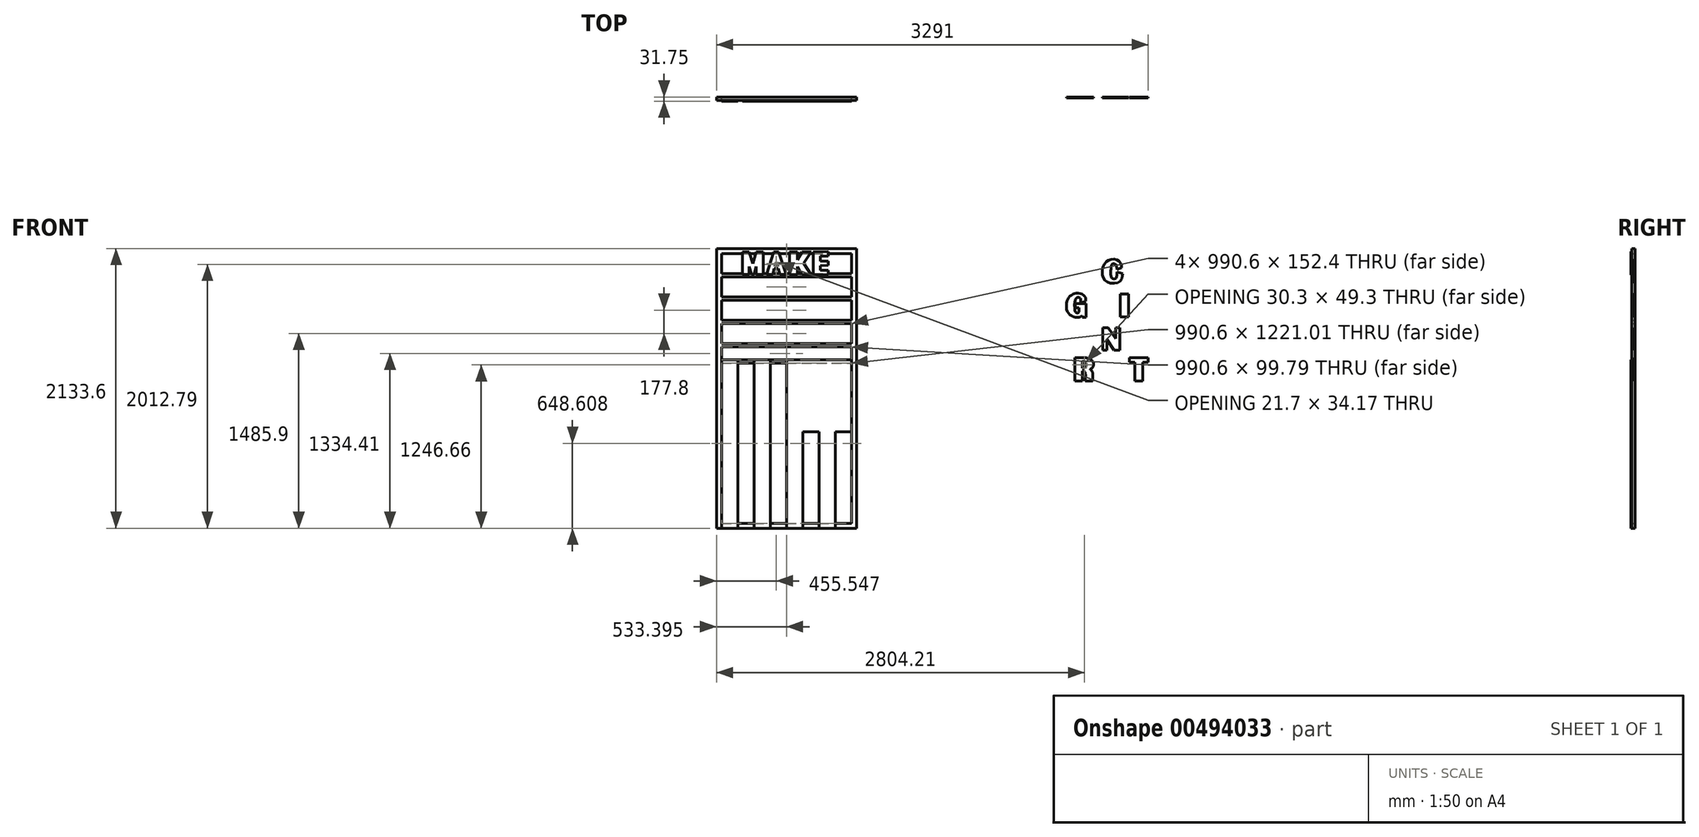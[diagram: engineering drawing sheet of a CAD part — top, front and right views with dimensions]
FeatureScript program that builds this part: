
annotation { "Feature Type Name" : "Feature", "Feature Type Description" : "" }
export const myFeature = defineFeature(function(context is Context, id is Id, definition is map)
    precondition{}
    {
        {
            var Q0;
            Q0=qCreatedBy(makeId("Front.planeOp"),FACE);
            var sketch = newSketch(context, id + "F0", { "sketchPlane" : qUnion([Q0])});
            skLineSegment(sketch, "E0.bottom", {"start": v(-657.23, 1067.61) * mm, "end": v(409.57, 1067.61) * mm});
            skLineSegment(sketch, "E0.top", {"start": v(-657.23, -1065.99) * mm, "end": v(409.58, -1065.99) * mm});
            skLineSegment(sketch, "E0.left", {"start": v(-657.23, 1067.61) * mm, "end": v(-657.23, -1065.99) * mm});
            skLineSegment(sketch, "E0.right", {"start": v(409.57, 1067.61) * mm, "end": v(409.57, -1065.99) * mm});
            skLineSegment(sketch, "E1.0", {"start": v(-619.13, 1029.51) * mm, "end": v(371.47, 1029.51) * mm});
            skLineSegment(sketch, "E1.1", {"start": v(-619.13, 1029.51) * mm, "end": v(-619.12, -1027.89) * mm});
            skLineSegment(sketch, "E1.2", {"start": v(-619.13, -1027.89) * mm, "end": v(371.48, -1027.89) * mm});
            skLineSegment(sketch, "E1.3", {"start": v(371.47, 1029.51) * mm, "end": v(371.47, -1027.89) * mm});
            skPoint(sketch, "E2.endSnap0", {"position": v(409.57, 0.81) * mm});
            skLineSegment(sketch, "E3", {"start": v(-619.13, 877.11) * mm, "end": v(371.47, 877.11) * mm});
            skLineSegment(sketch, "E4", {"start": v(371.47, 851.71) * mm, "end": v(-619.13, 851.71) * mm});
            skLineSegment(sketch, "E5", {"start": v(-619.13, 699.31) * mm, "end": v(371.47, 699.31) * mm});
            skLineSegment(sketch, "E6", {"start": v(-619.13, 673.91) * mm, "end": v(371.47, 673.91) * mm});
            skLineSegment(sketch, "E7", {"start": v(-619.13, 521.51) * mm, "end": v(371.47, 521.51) * mm});
            skLineSegment(sketch, "E8", {"start": v(-619.13, 496.11) * mm, "end": v(371.47, 496.11) * mm});
            skLineSegment(sketch, "E9", {"start": v(-619.13, 343.71) * mm, "end": v(371.47, 343.71) * mm});
            skLineSegment(sketch, "E10", {"start": v(-619.13, 318.31) * mm, "end": v(371.47, 318.31) * mm});
            skLineSegment(sketch, "E11", {"start": v(-619.13, 218.53) * mm, "end": v(371.47, 218.53) * mm});
            skPoint(sketch, "E12.startSnap0", {"position": v(-123.83, 1067.61) * mm});
            skLineSegment(sketch, "E13", {"start": v(-123.83, 218.53) * mm, "end": v(-123.83, -330.69) * mm});
            skLineSegment(sketch, "E14", {"start": v(-123.83, -330.69) * mm, "end": v(371.47, -330.69) * mm});
            skLineSegment(sketch, "E15", {"start": v(-619.12, 193.13) * mm, "end": v(-495.3, 193.13) * mm});
            skLineSegment(sketch, "E16", {"start": v(247.65, -330.69) * mm, "end": v(247.65, -1027.89) * mm});
            skLineSegment(sketch, "E17", {"start": v(-123.83, -330.69) * mm, "end": v(-123.82, -1027.89) * mm});
            skLineSegment(sketch, "E18", {"start": v(0, -330.69) * mm, "end": v(0, -1027.89) * mm});
            skLineSegment(sketch, "E19", {"start": v(123.82, -330.69) * mm, "end": v(123.83, -1027.89) * mm});
            skLineSegment(sketch, "E20", {"start": v(-247.65, 193.13) * mm, "end": v(-247.65, -1027.89) * mm});
            skLineSegment(sketch, "E21", {"start": v(-371.48, 193.13) * mm, "end": v(-371.47, -1027.89) * mm});
            skLineSegment(sketch, "E22", {"start": v(-495.3, 193.13) * mm, "end": v(-495.3, -1027.89) * mm});
            skLineSegment(sketch, "E23", {"start": v(-495.3, 193.13) * mm, "end": v(-495.3, 218.53) * mm});
            skLineSegment(sketch, "E24", {"start": v(-371.48, 193.13) * mm, "end": v(-371.48, 218.53) * mm});
            skLineSegment(sketch, "E25", {"start": v(-247.65, 193.13) * mm, "end": v(-247.65, 218.53) * mm});
            skPoint(sketch, "E26.orphan", {"position": v(-123.83, 193.13) * mm});
            skLineSegment(sketch, "E27.trimOffspring", {"start": v(-371.48, 193.13) * mm, "end": v(-247.65, 193.13) * mm});
            skLineSegment(sketch, "E28", {"start": v(-495.3, 193.13) * mm, "end": v(-371.48, 193.13) * mm});
            skLineSegment(sketch, "E29", {"start": v(-247.65, 193.13) * mm, "end": v(-123.83, 193.13) * mm});
            skLineSegment(sketch, "E30", {"start": v(-123.83, 193.13) * mm, "end": v(371.47, 193.13) * mm});
            skLineSegment(sketch, "E31", {"start": v(-619.12, -1027.89) * mm, "end": v(-619.12, -1065.99) * mm});
            skLineSegment(sketch, "E32", {"start": v(-495.3, -1027.89) * mm, "end": v(-495.3, -1065.99) * mm});
            skLineSegment(sketch, "E33", {"start": v(-371.47, -1027.89) * mm, "end": v(-371.47, -1065.99) * mm});
            skLineSegment(sketch, "E34", {"start": v(-247.65, -1027.89) * mm, "end": v(-247.65, -1065.99) * mm});
            skLineSegment(sketch, "E35", {"start": v(-123.83, -1027.89) * mm, "end": v(-123.83, -1065.99) * mm});
            skLineSegment(sketch, "E36", {"start": v(0, -1027.89) * mm, "end": v(0, -1065.99) * mm});
            skLineSegment(sketch, "E37", {"start": v(123.83, -1027.89) * mm, "end": v(123.83, -1065.99) * mm});
            skLineSegment(sketch, "E38", {"start": v(247.65, -1027.89) * mm, "end": v(247.65, -1065.99) * mm});
            skLineSegment(sketch, "E39", {"start": v(371.48, -1027.89) * mm, "end": v(371.48, -1065.99) * mm});
            skSolve(sketch);
        }
        {
            var Q0;
            Q0=makeQuery(id+"F0.imprint","IMPRINT",FACE,{"disambiguationData":[TD([[makeQuery(id+"F0.imprint","IMPRINT",EDGE,{"derivedFrom":sQuery(id+"F0.wireOp",EDGE,"E0.bottom")}),-1.0]])]});
            var Q1;
            {var subQ0=sQuery(id+"F0.wireOp",EDGE,"E3");Q1=makeQuery(id+"F0.imprint","IMPRINT",FACE,{"disambiguationData":[TD([[makeQuery(id+"F0.imprint","IMPRINT",EDGE,{"derivedFrom":subQ0}),-1.0]])]});}
            var Q2;
            {var subQ0=sQuery(id+"F0.wireOp",EDGE,"E5");Q2=makeQuery(id+"F0.imprint","IMPRINT",FACE,{"disambiguationData":[TD([[makeQuery(id+"F0.imprint","IMPRINT",EDGE,{"derivedFrom":subQ0}),-1.0]])]});}
            var Q3;
            {var subQ0=sQuery(id+"F0.wireOp",EDGE,"E7");Q3=makeQuery(id+"F0.imprint","IMPRINT",FACE,{"disambiguationData":[TD([[makeQuery(id+"F0.imprint","IMPRINT",EDGE,{"derivedFrom":subQ0}),-1.0]])]});}
            var Q4;
            {var subQ0=sQuery(id+"F0.wireOp",EDGE,"E9");Q4=makeQuery(id+"F0.imprint","IMPRINT",FACE,{"disambiguationData":[TD([[makeQuery(id+"F0.imprint","IMPRINT",EDGE,{"derivedFrom":subQ0}),-1.0]])]});}
            var Q5;
            {var subQ3=sQuery(id+"F0.wireOp",EDGE,"E15");Q5=makeQuery(id+"F0.imprint","IMPRINT",FACE,{"disambiguationData":[TD([[makeQuery(id+"F0.imprint","IMPRINT",EDGE,{"derivedFrom":subQ3}),1.0]])]});}
            var Q6;
            {var subQ0=sQuery(id+"F0.wireOp",EDGE,"E23");Q6=makeQuery(id+"F0.imprint","IMPRINT",FACE,{"disambiguationData":[TD([[makeQuery(id+"F0.imprint","IMPRINT",EDGE,{"derivedFrom":subQ0}),-1.0]])]});}
            var Q7;
            {var subQ0=sQuery(id+"F0.wireOp",EDGE,"E24");Q7=makeQuery(id+"F0.imprint","IMPRINT",FACE,{"disambiguationData":[TD([[makeQuery(id+"F0.imprint","IMPRINT",EDGE,{"derivedFrom":subQ0}),-1.0]])]});}
            var Q8;
            {var subQ3=sQuery(id+"F0.wireOp",EDGE,"E25");Q8=makeQuery(id+"F0.imprint","IMPRINT",FACE,{"disambiguationData":[TD([[makeQuery(id+"F0.imprint","IMPRINT",EDGE,{"derivedFrom":subQ3}),-1.0]])]});}
            var Q9;
            {var subQ3=sQuery(id+"F0.wireOp",EDGE,"E30");Q9=makeQuery(id+"F0.imprint","IMPRINT",FACE,{"disambiguationData":[TD([[makeQuery(id+"F0.imprint","IMPRINT",EDGE,{"derivedFrom":subQ3}),1.0]])]});}
            var Q10;
            {var subQ0=sQuery(id+"F0.wireOp",EDGE,"E38");Q10=makeQuery(id+"F0.imprint","IMPRINT",FACE,{"disambiguationData":[TD([[makeQuery(id+"F0.imprint","IMPRINT",EDGE,{"derivedFrom":subQ0}),1.0]])]});}
            var Q11;
            {var subQ0=sQuery(id+"F0.wireOp",EDGE,"E37");Q11=makeQuery(id+"F0.imprint","IMPRINT",FACE,{"disambiguationData":[TD([[makeQuery(id+"F0.imprint","IMPRINT",EDGE,{"derivedFrom":subQ0}),1.0]])]});}
            var Q12;
            {var subQ0=sQuery(id+"F0.wireOp",EDGE,"E36");Q12=makeQuery(id+"F0.imprint","IMPRINT",FACE,{"disambiguationData":[TD([[makeQuery(id+"F0.imprint","IMPRINT",EDGE,{"derivedFrom":subQ0}),1.0]])]});}
            var Q13;
            {var subQ0=sQuery(id+"F0.wireOp",EDGE,"E35");Q13=makeQuery(id+"F0.imprint","IMPRINT",FACE,{"disambiguationData":[TD([[makeQuery(id+"F0.imprint","IMPRINT",EDGE,{"derivedFrom":subQ0}),1.0]])]});}
            var Q14;
            {var subQ0=sQuery(id+"F0.wireOp",EDGE,"E34");Q14=makeQuery(id+"F0.imprint","IMPRINT",FACE,{"disambiguationData":[TD([[makeQuery(id+"F0.imprint","IMPRINT",EDGE,{"derivedFrom":subQ0}),1.0]])]});}
            var Q15;
            {var subQ0=sQuery(id+"F0.wireOp",EDGE,"E33");Q15=makeQuery(id+"F0.imprint","IMPRINT",FACE,{"disambiguationData":[TD([[makeQuery(id+"F0.imprint","IMPRINT",EDGE,{"derivedFrom":subQ0}),1.0]])]});}
            var Q16;
            {var subQ0=sQuery(id+"F0.wireOp",EDGE,"E32");Q16=makeQuery(id+"F0.imprint","IMPRINT",FACE,{"disambiguationData":[TD([[makeQuery(id+"F0.imprint","IMPRINT",EDGE,{"derivedFrom":subQ0}),1.0]])]});}
            var Q17;
            {var subQ0=sQuery(id+"F0.wireOp",EDGE,"E31");Q17=makeQuery(id+"F0.imprint","IMPRINT",FACE,{"disambiguationData":[TD([[makeQuery(id+"F0.imprint","IMPRINT",EDGE,{"derivedFrom":subQ0}),1.0]])]});}
            extrude(context, id + "F1", {"entities" : qUnion([Q0, Q1, Q2, Q3, Q4, Q5, Q6, Q7, Q8, Q9, Q10, Q11, Q12, Q13, Q14, Q15, Q16, Q17]), "depth" : 25.4 * mm});
        }
        {
            var Q0;
            Q0=makeQuery(id+"F1.opExtrude","CAP_FACE",FACE,{"disambiguationData":[OSD([sQuery(id+"F0.wireOp",EDGE,"E0.bottom"),sQuery(id+"F0.wireOp",EDGE,"E0.top"),sQuery(id+"F0.wireOp",EDGE,"E0.left"),sQuery(id+"F0.wireOp",EDGE,"E0.right"),sQuery(id+"F0.wireOp",EDGE,"E1.0"),sQuery(id+"F0.wireOp",EDGE,"E1.1"),sQuery(id+"F0.wireOp",EDGE,"E1.2"),sQuery(id+"F0.wireOp",EDGE,"E1.3"),sQuery(id+"F0.wireOp",EDGE,"E3"),sQuery(id+"F0.wireOp",EDGE,"E4"),sQuery(id+"F0.wireOp",EDGE,"E5"),sQuery(id+"F0.wireOp",EDGE,"E6"),sQuery(id+"F0.wireOp",EDGE,"E7"),sQuery(id+"F0.wireOp",EDGE,"E8"),sQuery(id+"F0.wireOp",EDGE,"E9"),sQuery(id+"F0.wireOp",EDGE,"E10"),sQuery(id+"F0.wireOp",EDGE,"E11"),sQuery(id+"F0.wireOp",EDGE,"E15"),sQuery(id+"F0.wireOp",EDGE,"E27.trimOffspring"),sQuery(id+"F0.wireOp",EDGE,"E28"),sQuery(id+"F0.wireOp",EDGE,"E29"),sQuery(id+"F0.wireOp",EDGE,"E30")])],"isStart":false});
            var sketch = newSketch(context, id + "F2", { "sketchPlane" : qUnion([Q0])});
            skPoint(sketch, "E40.0", {"position": v(-495.3, 193.13) * mm});
            skPoint(sketch, "E41.0", {"position": v(-371.48, 193.13) * mm});
            skPoint(sketch, "E42.0", {"position": v(-247.65, 193.13) * mm});
            skPoint(sketch, "E43.0", {"position": v(-123.83, 193.13) * mm});
            skPoint(sketch, "E44.0", {"position": v(-123.83, 218.53) * mm});
            skPoint(sketch, "E45.0", {"position": v(-247.65, 218.53) * mm});
            skPoint(sketch, "E46.0", {"position": v(-371.48, 218.53) * mm});
            skPoint(sketch, "E47.0", {"position": v(-495.3, 218.53) * mm});
            skPoint(sketch, "E48.0", {"position": v(371.47, 193.13) * mm});
            skPoint(sketch, "E49.0", {"position": v(371.47, 218.53) * mm});
            skPoint(sketch, "E50.0", {"position": v(371.48, -1027.89) * mm});
            skPoint(sketch, "E51.0", {"position": v(371.48, -1065.99) * mm});
            skPoint(sketch, "E52.0", {"position": v(247.65, -1027.89) * mm});
            skPoint(sketch, "E53.0", {"position": v(247.65, -1065.99) * mm});
            skPoint(sketch, "E54.0", {"position": v(123.83, -1065.99) * mm});
            skPoint(sketch, "E55.0", {"position": v(123.83, -1027.89) * mm});
            skPoint(sketch, "E56.0", {"position": v(0, -1065.99) * mm});
            skPoint(sketch, "E57.0", {"position": v(0, -1027.89) * mm});
            skPoint(sketch, "E58.0", {"position": v(-123.82, -1027.89) * mm});
            skPoint(sketch, "E59.0", {"position": v(-123.82, -1065.99) * mm});
            skPoint(sketch, "E60.0", {"position": v(-247.65, -1027.89) * mm});
            skPoint(sketch, "E61.0", {"position": v(-247.65, -1065.99) * mm});
            skPoint(sketch, "E62.0", {"position": v(-371.47, -1065.99) * mm});
            skPoint(sketch, "E63.0", {"position": v(-371.47, -1027.89) * mm});
            skPoint(sketch, "E64.0", {"position": v(-619.12, -1065.99) * mm});
            skPoint(sketch, "E65.0", {"position": v(-619.13, -1027.89) * mm});
            skPoint(sketch, "E66.0", {"position": v(-495.3, -1065.99) * mm});
            skPoint(sketch, "E67.0", {"position": v(-495.3, -1027.89) * mm});
            skPoint(sketch, "E68.0", {"position": v(-123.83, -330.69) * mm});
            skPoint(sketch, "E69.0", {"position": v(0, -330.69) * mm});
            skPoint(sketch, "E70.0", {"position": v(123.82, -330.69) * mm});
            skPoint(sketch, "E71.0", {"position": v(247.65, -330.69) * mm});
            skPoint(sketch, "E72.0", {"position": v(371.47, -330.69) * mm});
            skPoint(sketch, "E73.0", {"position": v(-619.12, 193.13) * mm});
            skPoint(sketch, "E74.0", {"position": v(-619.13, 218.53) * mm});
            skLineSegment(sketch, "E75", {"start": v(-123.83, 218.53) * mm, "end": v(-123.83, 193.13) * mm});
            skLineSegment(sketch, "E76", {"start": v(371.47, 218.53) * mm, "end": v(371.47, 193.13) * mm});
            skLineSegment(sketch, "E77", {"start": v(-247.65, 218.53) * mm, "end": v(-247.65, 193.13) * mm});
            skLineSegment(sketch, "E78", {"start": v(-371.48, 218.53) * mm, "end": v(-371.48, 193.13) * mm});
            skLineSegment(sketch, "E79", {"start": v(-495.3, 218.53) * mm, "end": v(-495.3, 193.13) * mm});
            skLineSegment(sketch, "E80", {"start": v(-619.13, 218.53) * mm, "end": v(-619.12, 193.13) * mm});
            skLineSegment(sketch, "E81", {"start": v(247.65, -1027.89) * mm, "end": v(247.65, -1065.99) * mm});
            skLineSegment(sketch, "E82", {"start": v(371.48, -1065.99) * mm, "end": v(371.48, -1027.89) * mm});
            skLineSegment(sketch, "E83", {"start": v(123.83, -1065.99) * mm, "end": v(123.83, -1027.89) * mm});
            skLineSegment(sketch, "E84", {"start": v(0, -1027.89) * mm, "end": v(0, -1065.99) * mm});
            skLineSegment(sketch, "E85", {"start": v(-123.82, -1065.99) * mm, "end": v(-123.82, -1027.89) * mm});
            skLineSegment(sketch, "E86", {"start": v(-247.65, -1027.89) * mm, "end": v(-247.65, -1065.99) * mm});
            skLineSegment(sketch, "E87", {"start": v(-371.47, -1065.99) * mm, "end": v(-371.47, -1027.89) * mm});
            skLineSegment(sketch, "E88", {"start": v(-495.3, -1027.89) * mm, "end": v(-495.3, -1065.99) * mm});
            skLineSegment(sketch, "E89", {"start": v(-619.13, -1065.99) * mm, "end": v(-619.13, -1027.89) * mm});
            skLineSegment(sketch, "E90", {"start": v(371.47, -330.69) * mm, "end": v(371.48, -1065.99) * mm});
            skLineSegment(sketch, "E91", {"start": v(247.65, -1065.99) * mm, "end": v(247.65, -330.69) * mm});
            skLineSegment(sketch, "E92", {"start": v(123.82, -330.69) * mm, "end": v(123.83, -1065.99) * mm});
            skLineSegment(sketch, "E93", {"start": v(0, -1065.99) * mm, "end": v(0, -330.69) * mm});
            skLineSegment(sketch, "E94", {"start": v(-123.82, -1065.99) * mm, "end": v(-123.83, 218.53) * mm});
            skLineSegment(sketch, "E95", {"start": v(-247.65, 218.53) * mm, "end": v(-247.65, -1065.99) * mm});
            skLineSegment(sketch, "E96", {"start": v(-371.47, -1065.99) * mm, "end": v(-371.48, 218.53) * mm});
            skLineSegment(sketch, "E97", {"start": v(-495.3, 218.53) * mm, "end": v(-495.3, -1065.99) * mm});
            skLineSegment(sketch, "E98", {"start": v(-123.83, -330.69) * mm, "end": v(371.47, -330.69) * mm});
            skLineSegment(sketch, "E99", {"start": v(371.47, -330.69) * mm, "end": v(371.47, 193.13) * mm});
            skLineSegment(sketch, "E100", {"start": v(371.47, 193.13) * mm, "end": v(-123.83, 193.13) * mm});
            skLineSegment(sketch, "E101", {"start": v(0, -330.69) * mm, "end": v(-123.83, -330.69) * mm});
            skLineSegment(sketch, "E102", {"start": v(123.82, -330.69) * mm, "end": v(247.65, -330.69) * mm});
            skLineSegment(sketch, "E103", {"start": v(-123.83, -330.69) * mm, "end": v(-123.82, -1065.99) * mm});
            skLineSegment(sketch, "E104", {"start": v(-123.82, -1065.99) * mm, "end": v(0, -1065.99) * mm});
            skLineSegment(sketch, "E105", {"start": v(123.83, -1065.99) * mm, "end": v(247.65, -1065.99) * mm});
            skLineSegment(sketch, "E106", {"start": v(247.65, -330.69) * mm, "end": v(123.82, -330.69) * mm});
            skLineSegment(sketch, "E107", {"start": v(-123.83, 218.53) * mm, "end": v(-123.83, -330.69) * mm});
            skLineSegment(sketch, "E108", {"start": v(-247.65, 218.53) * mm, "end": v(-371.48, 218.53) * mm});
            skLineSegment(sketch, "E109", {"start": v(-371.47, -1065.99) * mm, "end": v(-247.65, -1065.99) * mm});
            skLineSegment(sketch, "E110", {"start": v(-495.3, 218.53) * mm, "end": v(-619.13, 218.53) * mm});
            skLineSegment(sketch, "E111", {"start": v(-619.12, -1065.99) * mm, "end": v(-495.3, -1065.99) * mm});
            skLineSegment(sketch, "E112", {"start": v(-123.83, -361.45) * mm, "end": v(0, -361.45) * mm});
            skLineSegment(sketch, "E113", {"start": v(123.82, -360.14) * mm, "end": v(247.65, -360.14) * mm});
            skSolve(sketch);
        }
        {
            var Q0;
            {var subQ7=sQuery(id+"F2.wireOp",EDGE,"E99");Q0=makeQuery(id+"F2.imprint","IMPRINT",FACE,{"disambiguationData":[TD([[makeQuery(id+"F2.imprint","IMPRINT",EDGE,{"derivedFrom":subQ7}),-1.0]])]});}
            var Q1;
            {var subQ0=sQuery(id+"F2.wireOp",EDGE,"E76");Q1=makeQuery(id+"F2.imprint","IMPRINT",FACE,{"disambiguationData":[TD([[makeQuery(id+"F2.imprint","IMPRINT",EDGE,{"derivedFrom":subQ0}),-1.0]])]});}
            var Q2;
            {var subQ0=sQuery(id+"F2.wireOp",EDGE,"E112");Q2=makeQuery(id+"F2.imprint","IMPRINT",FACE,{"disambiguationData":[TD([[makeQuery(id+"F2.imprint","IMPRINT",EDGE,{"derivedFrom":subQ0}),-1.0]])]});}
            var Q3;
            {var subQ0=sQuery(id+"F2.wireOp",EDGE,"E104");Q3=makeQuery(id+"F2.imprint","IMPRINT",FACE,{"disambiguationData":[TD([[makeQuery(id+"F2.imprint","IMPRINT",EDGE,{"derivedFrom":subQ0}),1.0]])]});}
            var Q4;
            {var subQ0=sQuery(id+"F2.wireOp",EDGE,"E113");Q4=makeQuery(id+"F2.imprint","IMPRINT",FACE,{"disambiguationData":[TD([[makeQuery(id+"F2.imprint","IMPRINT",EDGE,{"derivedFrom":subQ0}),-1.0]])]});}
            var Q5;
            {var subQ0=sQuery(id+"F2.wireOp",EDGE,"E105");Q5=makeQuery(id+"F2.imprint","IMPRINT",FACE,{"disambiguationData":[TD([[makeQuery(id+"F2.imprint","IMPRINT",EDGE,{"derivedFrom":subQ0}),1.0]])]});}
            var Q6;
            {var subQ0=sQuery(id+"F2.wireOp",EDGE,"E108");Q6=makeQuery(id+"F2.imprint","IMPRINT",FACE,{"disambiguationData":[TD([[makeQuery(id+"F2.imprint","IMPRINT",EDGE,{"derivedFrom":subQ0}),-1.0]])]});}
            var Q7;
            {var subQ0=sQuery(id+"F2.wireOp",EDGE,"E109");Q7=makeQuery(id+"F2.imprint","IMPRINT",FACE,{"disambiguationData":[TD([[makeQuery(id+"F2.imprint","IMPRINT",EDGE,{"derivedFrom":subQ0}),1.0]])]});}
            var Q8;
            {var subQ0=sQuery(id+"F2.wireOp",EDGE,"E95");var subQ3=makeQuery(id+"F1.opExtrude","CAP_EDGE",EDGE,{"disambiguationData":[OSD([sQuery(id+"F0.wireOp",EDGE,"E1.2")])],"isStart":false});var subQ4=makeQuery(id+"F2.imprint","INTERSECT",VERTEX,{"derivedFrom":[subQ3,subQ0]});Q8=makeQuery(id+"F2.imprint","IMPRINT",FACE,{"disambiguationData":[TD([[makeQuery(id+"F2.imprint","IMPRINT",EDGE,{"disambiguationData":[TD([[subQ4,1.0]])],"derivedFrom":subQ3}),1.0]])]});}
            var Q9;
            {var subQ1=sQuery(id+"F0.wireOp",EDGE,"E15");var subQ7=sQuery(id+"F0.wireOp",EDGE,"E1.1");var subQ8=makeQuery(id+"F1.opExtrude","CAP_EDGE",EDGE,{"disambiguationData":[OSD([subQ7]),TDD([makeQuery(id+"F0.imprint","IMPRINT",EDGE,{"disambiguationData":[TD([[makeQuery(id+"F0.imprint","INTERSECT",VERTEX,{"derivedFrom":[subQ7,subQ1]}),-1.0]])],"derivedFrom":subQ7})])],"isStart":false});Q9=makeQuery(id+"F2.imprint","IMPRINT",FACE,{"disambiguationData":[TD([[makeQuery(id+"F2.imprint","IMPRINT",EDGE,{"derivedFrom":subQ8}),1.0]])]});}
            var Q10;
            {var subQ0=sQuery(id+"F2.wireOp",EDGE,"E89");Q10=makeQuery(id+"F2.imprint","IMPRINT",FACE,{"disambiguationData":[TD([[makeQuery(id+"F2.imprint","IMPRINT",EDGE,{"derivedFrom":subQ0}),-1.0]])]});}
            var Q11;
            {var subQ0=sQuery(id+"F2.wireOp",EDGE,"E80");Q11=makeQuery(id+"F2.imprint","IMPRINT",FACE,{"disambiguationData":[TD([[makeQuery(id+"F2.imprint","IMPRINT",EDGE,{"derivedFrom":subQ0}),1.0]])]});}
            extrude(context, id + "F3", {"entities" : qUnion([Q0, Q1, Q2, Q3, Q4, Q5, Q6, Q7, Q8, Q9, Q10, Q11]), "depth" : 6.35 * mm});
        }
        {
            var Q0;
            Q0=makeQuery(id+"F3.opExtrude","CAP_FACE",FACE,{"disambiguationData":[OSD([sQuery(id+"F0.wireOp",EDGE,"E11"),sQuery(id+"F2.wireOp",EDGE,"E76"),sQuery(id+"F2.wireOp",EDGE,"E107"),sQuery(id+"F2.wireOp",EDGE,"E98"),sQuery(id+"F2.wireOp",EDGE,"E99")])],"isStart":false});
            var sketch = newSketch(context, id + "F4", { "sketchPlane" : qUnion([Q0])});
            skPoint(sketch, "E114.0", {"position": v(-123.83, -330.69) * mm});
            skPoint(sketch, "E115.0", {"position": v(-123.83, -361.45) * mm});
            skPoint(sketch, "E116.0", {"position": v(0, -361.45) * mm});
            skLineSegment(sketch, "E117.0", {"start": v(-123.83, -330.69) * mm, "end": v(371.47, -330.69) * mm});
            skPoint(sketch, "E118.0", {"position": v(123.82, -360.14) * mm});
            skPoint(sketch, "E119.0", {"position": v(247.65, -360.14) * mm});
            skLineSegment(sketch, "E120", {"start": v(-123.83, -330.69) * mm, "end": v(-123.83, -361.45) * mm});
            skLineSegment(sketch, "E121", {"start": v(-123.83, -361.45) * mm, "end": v(0, -361.45) * mm});
            skLineSegment(sketch, "E122", {"start": v(0, -361.45) * mm, "end": v(0, -330.69) * mm});
            skLineSegment(sketch, "E123", {"start": v(0, -330.69) * mm, "end": v(-123.83, -330.69) * mm});
            skLineSegment(sketch, "E124", {"start": v(123.82, -360.14) * mm, "end": v(123.82, -330.69) * mm});
            skLineSegment(sketch, "E125", {"start": v(123.82, -360.14) * mm, "end": v(247.65, -360.14) * mm});
            skLineSegment(sketch, "E126", {"start": v(247.65, -360.14) * mm, "end": v(247.65, -330.69) * mm});
            skLineSegment(sketch, "E127", {"start": v(247.65, -330.69) * mm, "end": v(123.82, -330.69) * mm});
            skSolve(sketch);
        }
        {
            var Q0;
            Q0=makeQuery(id+"F4.imprint","IMPRINT",FACE,{"disambiguationData":[TD([[makeQuery(id+"F4.imprint","IMPRINT",EDGE,{"derivedFrom":sQuery(id+"F4.wireOp",EDGE,"E120")}),1.0]])]});
            extrude(context, id + "F5", {"entities" : qUnion([Q0]), "operationType" : NewBodyOperationType.ADD, "oppositeDirection" : true, "depth" : 6.35 * mm});
        }
        {
            var Q0;
            Q0=makeQuery(id+"F3.opExtrude","CAP_FACE",FACE,{"disambiguationData":[OSD([sQuery(id+"F0.wireOp",EDGE,"E11"),sQuery(id+"F2.wireOp",EDGE,"E76"),sQuery(id+"F2.wireOp",EDGE,"E107"),sQuery(id+"F2.wireOp",EDGE,"E98"),sQuery(id+"F2.wireOp",EDGE,"E99")])],"isStart":false});
            var sketch = newSketch(context, id + "F6", { "sketchPlane" : qUnion([Q0])});
            skPoint(sketch, "E128.0", {"position": v(123.82, -360.14) * mm});
            skPoint(sketch, "E129.0", {"position": v(247.65, -360.14) * mm});
            skLineSegment(sketch, "E130.0", {"start": v(-123.83, -330.69) * mm, "end": v(371.47, -330.69) * mm});
            skLineSegment(sketch, "E131", {"start": v(123.82, -360.14) * mm, "end": v(123.82, -330.69) * mm});
            skLineSegment(sketch, "E132", {"start": v(247.65, -360.14) * mm, "end": v(247.65, -330.69) * mm});
            skLineSegment(sketch, "E133", {"start": v(247.65, -330.69) * mm, "end": v(123.82, -330.69) * mm});
            skLineSegment(sketch, "E134", {"start": v(123.82, -360.14) * mm, "end": v(247.65, -360.14) * mm});
            skSolve(sketch);
        }
        {
            var Q0;
            Q0 = qSketchRegion(id + "F6", true);
            extrude(context, id + "F7", {"entities" : qUnion([Q0]), "operationType" : NewBodyOperationType.ADD, "oppositeDirection" : true, "depth" : 6.35 * mm});
        }
        {
            var Q0;
            Q0=qCreatedBy(makeId("Front.planeOp"),FACE);
            var sketch = newSketch(context, id + "F8", { "sketchPlane" : qUnion([Q0])});
            skLineSegment(sketch, "E135", {"start": v(2039.4, 464.61) * mm, "end": v(2091.67, 464.61) * mm});
            skLineSegment(sketch, "E136", {"start": v(2091.67, 464.61) * mm, "end": v(2117.8, 375.8) * mm});
            skLineSegment(sketch, "E137", {"start": v(2117.8, 375.8) * mm, "end": v(2143.94, 464.61) * mm});
            skLineSegment(sketch, "E138", {"start": v(2143.94, 464.61) * mm, "end": v(2198.45, 464.61) * mm});
            skLineSegment(sketch, "E139", {"start": v(2198.45, 464.61) * mm, "end": v(2198.45, 293.67) * mm});
            skLineSegment(sketch, "E140", {"start": v(2198.45, 293.67) * mm, "end": v(2143.94, 293.67) * mm});
            skLineSegment(sketch, "E141", {"start": v(2143.94, 293.67) * mm, "end": v(2143.94, 354.4) * mm});
            skLineSegment(sketch, "E142", {"start": v(2143.94, 354.4) * mm, "end": v(2129.18, 293.67) * mm});
            skLineSegment(sketch, "E143", {"start": v(2129.18, 293.67) * mm, "end": v(2110.64, 293.67) * mm});
            skLineSegment(sketch, "E144", {"start": v(2039.4, 464.61) * mm, "end": v(2039.4, 293.67) * mm});
            skLineSegment(sketch, "E145", {"start": v(2039.4, 293.67) * mm, "end": v(2091.67, 293.67) * mm});
            skLineSegment(sketch, "E146", {"start": v(2091.67, 293.67) * mm, "end": v(2091.67, 354.4) * mm});
            skLineSegment(sketch, "E147", {"start": v(2091.67, 354.4) * mm, "end": v(2110.64, 293.67) * mm});
            skLineSegment(sketch, "E148", {"start": v(1938.85, 980.5) * mm, "end": v(1899.6, 980.5) * mm});
            skLineSegment(sketch, "E149", {"start": v(1899.6, 980.5) * mm, "end": v(1845.11, 807.8) * mm});
            skLineSegment(sketch, "E150", {"start": v(1919.23, 980.5) * mm, "end": v(1919.23, 769.93) * mm, "construction": true});
            skLineSegment(sketch, "E151", {"start": v(1938.85, 980.5) * mm, "end": v(1993.34, 807.8) * mm});
            skLineSegment(sketch, "E152", {"start": v(1934.24, 853.05) * mm, "end": v(1919.23, 853.05) * mm});
            skLineSegment(sketch, "E153", {"start": v(1934.24, 853.05) * mm, "end": v(1946.7, 807.8) * mm});
            skLineSegment(sketch, "E154", {"start": v(1946.7, 807.8) * mm, "end": v(1993.34, 807.8) * mm});
            skLineSegment(sketch, "E155", {"start": v(1919.23, 868.75) * mm, "end": v(1930.08, 868.75) * mm});
            skLineSegment(sketch, "E156", {"start": v(1930.08, 868.75) * mm, "end": v(1919.23, 902.92) * mm});
            skLineSegment(sketch, "E157.MirrorCS", {"start": v(1908.38, 868.75) * mm, "end": v(1919.23, 902.92) * mm});
            skLineSegment(sketch, "E158.MirrorCS", {"start": v(1919.23, 868.75) * mm, "end": v(1908.38, 868.75) * mm});
            skLineSegment(sketch, "E159.MirrorCS", {"start": v(1904.22, 853.05) * mm, "end": v(1919.23, 853.05) * mm});
            skLineSegment(sketch, "E160.MirrorCS", {"start": v(1904.22, 853.05) * mm, "end": v(1891.75, 807.8) * mm});
            skLineSegment(sketch, "E161.MirrorCS", {"start": v(1891.75, 807.8) * mm, "end": v(1845.11, 807.8) * mm});
            skLineSegment(sketch, "E162", {"start": v(2685.35, 721.41) * mm, "end": v(2685.35, 546.4) * mm});
            skLineSegment(sketch, "E163", {"start": v(2685.35, 546.4) * mm, "end": v(2747.39, 546.4) * mm});
            skLineSegment(sketch, "E164", {"start": v(2747.39, 546.4) * mm, "end": v(2747.39, 607.78) * mm});
            skLineSegment(sketch, "E165", {"start": v(2747.39, 607.78) * mm, "end": v(2781.35, 546.4) * mm});
            skLineSegment(sketch, "E166", {"start": v(2781.35, 546.4) * mm, "end": v(2849.92, 546.4) * mm});
            skLineSegment(sketch, "E167", {"start": v(2685.35, 633.9) * mm, "end": v(2886.5, 633.9) * mm, "construction": true});
            skLineSegment(sketch, "E168", {"start": v(2849.92, 546.4) * mm, "end": v(2795.06, 633.9) * mm});
            skLineSegment(sketch, "E169.MirrorCS", {"start": v(2685.35, 721.41) * mm, "end": v(2747.39, 721.41) * mm});
            skLineSegment(sketch, "E170.MirrorCS", {"start": v(2747.39, 721.41) * mm, "end": v(2747.39, 660.03) * mm});
            skLineSegment(sketch, "E171.MirrorCS", {"start": v(2747.39, 660.03) * mm, "end": v(2781.35, 721.41) * mm});
            skLineSegment(sketch, "E172.MirrorCS", {"start": v(2781.35, 721.41) * mm, "end": v(2849.92, 721.41) * mm});
            skLineSegment(sketch, "E173.MirrorCS", {"start": v(2849.92, 721.41) * mm, "end": v(2795.06, 633.9) * mm});
            skLineSegment(sketch, "E174", {"start": v(2073.72, 234.3) * mm, "end": v(2073.72, 56.01) * mm});
            skLineSegment(sketch, "E175", {"start": v(2073.72, 56.01) * mm, "end": v(2131.84, 56.01) * mm});
            skLineSegment(sketch, "E176", {"start": v(2131.84, 56.01) * mm, "end": v(2131.84, 134.38) * mm});
            skLineSegment(sketch, "E177", {"start": v(2153.4, 56.01) * mm, "end": v(2210.2, 56.01) * mm});
            skLineSegment(sketch, "E178", {"start": v(2210.2, 56.01) * mm, "end": v(2210.2, 114.79) * mm});
            skFitSpline(sketch, "E179", {"points": [v(2131.84, 134.38) * mm, v(2149.82, 128.75) * mm, v(2153.4, 56.01) * mm], "startDerivative": vector(61.08, -1.09) * mm, "endDerivative": vector(-10.32, -138.32) * mm});
            skArc(sketch, "E180", {"start": v(2210.2, 114.79) * mm, "mid": v(2205, 133.06) * mm, "end": v(2190.92, 145.83) * mm});
            skLineSegment(sketch, "E181", {"start": v(2073.72, 234.3) * mm, "end": v(2155.35, 234.3) * mm});
            skFitSpline(sketch, "E182", {"points": [v(2155.35, 234.3) * mm, v(2174.29, 230.77) * mm, v(2196.82, 220.97) * mm, v(2212.17, 204.97) * mm, v(2217.4, 183.1) * mm, v(2208.9, 160.24) * mm, v(2190.92, 145.83) * mm], "startDerivative": vector(120.9, 0) * mm, "endDerivative": vector(-117.4, -73.8) * mm});
            skLineSegment(sketch, "E183", {"start": v(2419.6, 721.77) * mm, "end": v(2419.6, 546.75) * mm});
            skLineSegment(sketch, "E184", {"start": v(2419.6, 546.75) * mm, "end": v(2482.4, 546.75) * mm});
            skLineSegment(sketch, "E185", {"start": v(2482.4, 546.75) * mm, "end": v(2482.4, 722.23) * mm});
            skLineSegment(sketch, "E186", {"start": v(2482.4, 722.23) * mm, "end": v(2419.6, 721.77) * mm});
            skLineSegment(sketch, "E187", {"start": v(2395.3, 888.23) * mm, "end": v(2437.8, 877.61) * mm});
            skFitSpline(sketch, "E188", {"points": [v(2429.48, 922.4) * mm, v(2429.48, 943.18) * mm, v(2412.4, 969.97) * mm, v(2388.38, 984.28) * mm, v(2351.9, 985.67) * mm, v(2324.2, 974.59) * mm, v(2298.8, 947.8) * mm, v(2286.33, 917.32) * mm, v(2283.55, 880.38) * mm, v(2291.4, 844.36) * mm, v(2318.19, 813.42) * mm, v(2371.76, 802.8) * mm, v(2420.24, 818.96) * mm, v(2436.4, 851.29) * mm, v(2437.8, 877.61) * mm], "startDerivative": vector(54.98, 366.17) * mm, "endDerivative": vector(-8.03, 408.66) * mm});
            skPoint(sketch, "E189.1.internal.orphan", {"position": v(2393.46, 927.02) * mm});
            skPoint(sketch, "E190.start.orphan", {"position": v(2393.46, 908.09) * mm});
            skFitSpline(sketch, "E191", {"points": [v(2393.46, 908.09) * mm, v(2393.46, 927.02) * mm, v(2387.92, 943.65) * mm, v(2375.45, 952.42) * mm, v(2366.21, 951.96) * mm, v(2355.6, 943.65) * mm, v(2349.13, 908.09) * mm, v(2347.28, 880.84) * mm, v(2352.36, 848.52) * mm, v(2365.75, 837.43) * mm, v(2379.14, 836.97) * mm, v(2388.84, 844.82) * mm, v(2393.46, 861.45) * mm, v(2395.3, 888.23) * mm], "startDerivative": vector(12.21, 248.32) * mm, "endDerivative": vector(14.29, 307.11) * mm});
            skLineSegment(sketch, "E192", {"start": v(2393.46, 908.09) * mm, "end": v(2429.48, 922.4) * mm});
            skLineSegment(sketch, "E193", {"start": v(2131.84, 156.02) * mm, "end": v(2131.84, 205.32) * mm});
            skArc(sketch, "E194", {"start": v(2131.84, 156.02) * mm, "mid": v(2162.14, 180.67) * mm, "end": v(2131.84, 205.32) * mm});
            skLineSegment(sketch, "E195", {"start": v(2743.93, 981.4) * mm, "end": v(2743.93, 894.13) * mm});
            skLineSegment(sketch, "E196", {"start": v(2743.93, 981.4) * mm, "end": v(2858.46, 981.4) * mm});
            skLineSegment(sketch, "E197", {"start": v(2858.46, 982.33) * mm, "end": v(2858.46, 947.7) * mm});
            skLineSegment(sketch, "E198", {"start": v(2858.46, 947.7) * mm, "end": v(2798.42, 947.7) * mm});
            skLineSegment(sketch, "E199", {"start": v(2798.42, 947.7) * mm, "end": v(2798.42, 911.67) * mm});
            skLineSegment(sketch, "E200", {"start": v(2798.42, 911.67) * mm, "end": v(2858.46, 911.67) * mm});
            skLineSegment(sketch, "E201", {"start": v(2858.92, 911.21) * mm, "end": v(2858.92, 894.13) * mm});
            skLineSegment(sketch, "E202.MirrorCS", {"start": v(2743.93, 806.85) * mm, "end": v(2858.46, 806.85) * mm});
            skLineSegment(sketch, "E203.MirrorCS", {"start": v(2858.46, 840.56) * mm, "end": v(2798.42, 840.56) * mm});
            skLineSegment(sketch, "E204.MirrorCS", {"start": v(2858.46, 805.92) * mm, "end": v(2858.46, 840.56) * mm});
            skLineSegment(sketch, "E205.MirrorCS", {"start": v(2798.42, 840.56) * mm, "end": v(2798.42, 876.58) * mm});
            skLineSegment(sketch, "E206.MirrorCS", {"start": v(2798.42, 876.58) * mm, "end": v(2858.46, 876.58) * mm});
            skLineSegment(sketch, "E207.MirrorCS", {"start": v(2858.92, 877.04) * mm, "end": v(2858.92, 894.13) * mm});
            skLineSegment(sketch, "E208", {"start": v(2743.93, 894.13) * mm, "end": v(2743.93, 806.85) * mm});
            skLineSegment(sketch, "E209", {"start": v(2743.93, 981.4) * mm, "end": v(2743.93, 806.85) * mm});
            skLineSegment(sketch, "E210", {"start": v(2858.46, 806.85) * mm, "end": v(2858.46, 840.56) * mm});
            skLineSegment(sketch, "E211", {"start": v(2858.92, 877.04) * mm, "end": v(2858.92, 911.21) * mm});
            skLineSegment(sketch, "E212", {"start": v(2858.92, 911.21) * mm, "end": v(2798.42, 911.67) * mm});
            skLineSegment(sketch, "E213", {"start": v(2798.42, 911.67) * mm, "end": v(2798.42, 947.7) * mm});
            skLineSegment(sketch, "E214", {"start": v(2798.42, 947.7) * mm, "end": v(2858.46, 947.7) * mm});
            skLineSegment(sketch, "E215", {"start": v(2858.46, 947.7) * mm, "end": v(2858.46, 982.33) * mm});
            skLineSegment(sketch, "E216", {"start": v(2858.46, 982.33) * mm, "end": v(2743.93, 981.4) * mm});
            skLineSegment(sketch, "E217", {"start": v(2798.42, 876.58) * mm, "end": v(2858.92, 877.04) * mm});
            skLineSegment(sketch, "E218", {"start": v(2489.8, 235.65) * mm, "end": v(2633.78, 235.65) * mm});
            skLineSegment(sketch, "E219", {"start": v(2633.78, 235.65) * mm, "end": v(2633.78, 199.96) * mm});
            skLineSegment(sketch, "E220", {"start": v(2633.78, 199.96) * mm, "end": v(2592.51, 199.96) * mm});
            skLineSegment(sketch, "E221", {"start": v(2592.51, 199.96) * mm, "end": v(2592.51, 56.92) * mm});
            skLineSegment(sketch, "E222", {"start": v(2592.51, 56.92) * mm, "end": v(2532.5, 56.92) * mm});
            skLineSegment(sketch, "E223", {"start": v(2532.5, 56.92) * mm, "end": v(2532.5, 199.96) * mm});
            skLineSegment(sketch, "E224", {"start": v(2532.5, 199.96) * mm, "end": v(2489.8, 199.96) * mm});
            skLineSegment(sketch, "E225", {"start": v(2489.8, 199.96) * mm, "end": v(2489.8, 235.65) * mm});
            skLineSegment(sketch, "E226", {"start": v(2285.67, 465.43) * mm, "end": v(2285.67, 293.33) * mm});
            skLineSegment(sketch, "E227", {"start": v(2285.67, 293.33) * mm, "end": v(2319.43, 293.33) * mm});
            skLineSegment(sketch, "E228", {"start": v(2319.43, 293.33) * mm, "end": v(2319.43, 376.33) * mm});
            skLineSegment(sketch, "E229", {"start": v(2319.43, 376.33) * mm, "end": v(2372.88, 293.33) * mm});
            skLineSegment(sketch, "E230", {"start": v(2372.88, 293.33) * mm, "end": v(2417.9, 293.33) * mm});
            skLineSegment(sketch, "E231", {"start": v(2417.9, 293.33) * mm, "end": v(2417.9, 465.43) * mm});
            skLineSegment(sketch, "E232", {"start": v(2417.9, 465.43) * mm, "end": v(2384.13, 465.43) * mm});
            skLineSegment(sketch, "E233", {"start": v(2384.13, 465.43) * mm, "end": v(2384.13, 380.55) * mm});
            skLineSegment(sketch, "E234", {"start": v(2384.13, 380.55) * mm, "end": v(2328.8, 465.43) * mm});
            skFitSpline(sketch, "E235", {"points": [v(2157.55, 668.28) * mm, v(2157.08, 687.97) * mm, v(2147.23, 706.26) * mm, v(2128.47, 719.86) * mm, v(2108.3, 725.48) * mm, v(2079.7, 725.95) * mm, v(2061.89, 720.33) * mm, v(2040.32, 707.67) * mm, v(2024.84, 688.9) * mm, v(2014.53, 665) * mm, v(2010.3, 634.51) * mm, v(2011.71, 600.28) * mm, v(2027.19, 571.2) * mm, v(2047.35, 555.27) * mm], "startDerivative": vector(20.94, 293.44) * mm, "endDerivative": vector(270.9, -177.33) * mm});
            skFitSpline(sketch, "E236", {"points": [v(2047.35, 555.27) * mm, v(2067.98, 545.89) * mm, v(2089.08, 543.54) * mm, v(2114.87, 546.36) * mm, v(2130.82, 555.27) * mm], "startDerivative": vector(81.05, -43.5) * mm, "endDerivative": vector(63.19, 45.24) * mm});
            skLineSegment(sketch, "E237", {"start": v(2117.22, 651.4) * mm, "end": v(2157.55, 668.28) * mm});
            skLineSegment(sketch, "E238", {"start": v(2117.22, 651.4) * mm, "end": v(2117.22, 683.75) * mm});
            skFitSpline(sketch, "E239", {"points": [v(2117.22, 683.75) * mm, v(2112.06, 692.2) * mm, v(2103.62, 695.47) * mm, v(2091.9, 694.07) * mm, v(2082.05, 683.75) * mm, v(2076.42, 671.56) * mm, v(2073.14, 649.05) * mm, v(2072.67, 629.82) * mm, v(2073.14, 610.6) * mm, v(2074.08, 594.19) * mm, v(2080.64, 583.87) * mm, v(2088.62, 576.84) * mm, v(2095.65, 575.9) * mm, v(2102.21, 580.59) * mm, v(2105.5, 585.28) * mm], "startDerivative": vector(-67.72, 150.52) * mm, "endDerivative": vector(57.4, 95.01) * mm});
            skLineSegment(sketch, "E240", {"start": v(2105.5, 585.28) * mm, "end": v(2105.5, 615.29) * mm});
            skLineSegment(sketch, "E241", {"start": v(2105.5, 615.29) * mm, "end": v(2078.3, 615.29) * mm});
            skLineSegment(sketch, "E242", {"start": v(2078.3, 615.29) * mm, "end": v(2078.3, 647.64) * mm});
            skLineSegment(sketch, "E243", {"start": v(2078.3, 647.64) * mm, "end": v(2160.36, 647.64) * mm});
            skLineSegment(sketch, "E244", {"start": v(2160.36, 647.64) * mm, "end": v(2160.36, 543.54) * mm});
            skLineSegment(sketch, "E245", {"start": v(2160.36, 543.54) * mm, "end": v(2130.82, 543.54) * mm});
            skLineSegment(sketch, "E246", {"start": v(2130.82, 543.54) * mm, "end": v(2130.82, 555.27) * mm});
            skLineSegment(sketch, "E247", {"start": v(2285.67, 465.43) * mm, "end": v(2328.8, 465.43) * mm});
            skSolve(sketch);
        }
        {
            var Q0;
            Q0 = qSketchRegion(id + "F8", true);
            extrude(context, id + "F9", {"entities" : qUnion([Q0]), "depth" : 6.35 * mm});
        }
        {
            var Q0;
            Q0=makeQuery(id+"F9.opExtrude","SWEPT_BODY",BODY,{"disambiguationData":[OSD([sQuery(id+"F8.wireOp",EDGE,"E135"),sQuery(id+"F8.wireOp",EDGE,"E136"),sQuery(id+"F8.wireOp",EDGE,"E137"),sQuery(id+"F8.wireOp",EDGE,"E138"),sQuery(id+"F8.wireOp",EDGE,"E139"),sQuery(id+"F8.wireOp",EDGE,"E140"),sQuery(id+"F8.wireOp",EDGE,"E141"),sQuery(id+"F8.wireOp",EDGE,"E142"),sQuery(id+"F8.wireOp",EDGE,"E143"),sQuery(id+"F8.wireOp",EDGE,"E144"),sQuery(id+"F8.wireOp",EDGE,"E145"),sQuery(id+"F8.wireOp",EDGE,"E146"),sQuery(id+"F8.wireOp",EDGE,"E147")])]});
            transform(context, id + "F10", {"entities" : qUnion([Q0]), "transformType" : TransformType.TRANSLATION_3D, "dx" : -2499.36 * mm, "dy" : -25.4 * mm, "dz" : 576.58 * mm, "makeCopy" : false});
        }
        {
            var Q0;
            Q0=makeQuery(id+"F9.opExtrude","SWEPT_BODY",BODY,{"disambiguationData":[OSD([sQuery(id+"F8.wireOp",EDGE,"E148"),sQuery(id+"F8.wireOp",EDGE,"E149"),sQuery(id+"F8.wireOp",EDGE,"E151"),sQuery(id+"F8.wireOp",EDGE,"E152"),sQuery(id+"F8.wireOp",EDGE,"E153"),sQuery(id+"F8.wireOp",EDGE,"E154"),sQuery(id+"F8.wireOp",EDGE,"E155"),sQuery(id+"F8.wireOp",EDGE,"E156"),sQuery(id+"F8.wireOp",EDGE,"E157.MirrorCS"),sQuery(id+"F8.wireOp",EDGE,"E158.MirrorCS"),sQuery(id+"F8.wireOp",EDGE,"E159.MirrorCS"),sQuery(id+"F8.wireOp",EDGE,"E160.MirrorCS"),sQuery(id+"F8.wireOp",EDGE,"E161.MirrorCS")])]});
            transform(context, id + "F11", {"entities" : qUnion([Q0]), "transformType" : TransformType.TRANSLATION_3D, "dx" : -2120.9 * mm, "dy" : -25.4 * mm, "dz" : 60.96 * mm, "makeCopy" : false});
        }
        {
            var Q0;
            Q0=makeQuery(id+"F9.opExtrude","SWEPT_BODY",BODY,{"disambiguationData":[OSD([sQuery(id+"F8.wireOp",EDGE,"E162"),sQuery(id+"F8.wireOp",EDGE,"E163"),sQuery(id+"F8.wireOp",EDGE,"E164"),sQuery(id+"F8.wireOp",EDGE,"E165"),sQuery(id+"F8.wireOp",EDGE,"E166"),sQuery(id+"F8.wireOp",EDGE,"E168"),sQuery(id+"F8.wireOp",EDGE,"E169.MirrorCS"),sQuery(id+"F8.wireOp",EDGE,"E170.MirrorCS"),sQuery(id+"F8.wireOp",EDGE,"E171.MirrorCS"),sQuery(id+"F8.wireOp",EDGE,"E172.MirrorCS"),sQuery(id+"F8.wireOp",EDGE,"E173.MirrorCS")])]});
            transform(context, id + "F12", {"entities" : qUnion([Q0]), "transformType" : TransformType.TRANSLATION_3D, "dx" : -2786.38 * mm, "dy" : -25.4 * mm, "dz" : 320.04 * mm, "makeCopy" : false});
        }
        {
            var Q0;
            Q0=makeQuery(id+"F9.opExtrude","SWEPT_BODY",BODY,{"disambiguationData":[OSD([sQuery(id+"F8.wireOp",EDGE,"E202.MirrorCS"),sQuery(id+"F8.wireOp",EDGE,"E203.MirrorCS"),sQuery(id+"F8.wireOp",EDGE,"E211"),sQuery(id+"F8.wireOp",EDGE,"E209"),sQuery(id+"F8.wireOp",EDGE,"E210"),sQuery(id+"F8.wireOp",EDGE,"E205.MirrorCS"),sQuery(id+"F8.wireOp",EDGE,"E217"),sQuery(id+"F8.wireOp",EDGE,"E212"),sQuery(id+"F8.wireOp",EDGE,"E213"),sQuery(id+"F8.wireOp",EDGE,"E214"),sQuery(id+"F8.wireOp",EDGE,"E215"),sQuery(id+"F8.wireOp",EDGE,"E216")])]});
            transform(context, id + "F13", {"entities" : qUnion([Q0]), "transformType" : TransformType.TRANSLATION_3D, "dx" : -2664.46 * mm, "dy" : -25.4 * mm, "dz" : 58.42 * mm, "makeCopy" : false});
        }
        {
            var Q0;
            Q0=makeQuery(id+"F9.opExtrude","SWEPT_BODY",BODY,{"disambiguationData":[OSD([sQuery(id+"F8.wireOp",EDGE,"E162"),sQuery(id+"F8.wireOp",EDGE,"E163"),sQuery(id+"F8.wireOp",EDGE,"E164"),sQuery(id+"F8.wireOp",EDGE,"E165"),sQuery(id+"F8.wireOp",EDGE,"E166"),sQuery(id+"F8.wireOp",EDGE,"E168"),sQuery(id+"F8.wireOp",EDGE,"E169.MirrorCS"),sQuery(id+"F8.wireOp",EDGE,"E170.MirrorCS"),sQuery(id+"F8.wireOp",EDGE,"E171.MirrorCS"),sQuery(id+"F8.wireOp",EDGE,"E172.MirrorCS"),sQuery(id+"F8.wireOp",EDGE,"E173.MirrorCS")])]});
            transform(context, id + "F14", {"entities" : qUnion([Q0]), "transformType" : TransformType.TRANSLATION_3D, "dx" : 0 * mm, "dy" : 0 * mm, "dz" : 3.8 * mm, "makeCopy" : false});
        }
        {
            var Q0;
            Q0=makeQuery(id+"F9.opExtrude","SWEPT_BODY",BODY,{"disambiguationData":[OSD([sQuery(id+"F8.wireOp",EDGE,"E162"),sQuery(id+"F8.wireOp",EDGE,"E163"),sQuery(id+"F8.wireOp",EDGE,"E164"),sQuery(id+"F8.wireOp",EDGE,"E165"),sQuery(id+"F8.wireOp",EDGE,"E166"),sQuery(id+"F8.wireOp",EDGE,"E168"),sQuery(id+"F8.wireOp",EDGE,"E169.MirrorCS"),sQuery(id+"F8.wireOp",EDGE,"E170.MirrorCS"),sQuery(id+"F8.wireOp",EDGE,"E171.MirrorCS"),sQuery(id+"F8.wireOp",EDGE,"E172.MirrorCS"),sQuery(id+"F8.wireOp",EDGE,"E173.MirrorCS")])]});
            transform(context, id + "F15", {"entities" : qUnion([Q0]), "transformType" : TransformType.TRANSLATION_3D, "dx" : 0 * mm, "dy" : 0 * mm, "dz" : -2.03 * mm, "makeCopy" : false});
        }
        {
            var Q0;
            Q0=makeQuery(id+"F9.opExtrude","SWEPT_BODY",BODY,{"disambiguationData":[OSD([sQuery(id+"F8.wireOp",EDGE,"E202.MirrorCS"),sQuery(id+"F8.wireOp",EDGE,"E203.MirrorCS"),sQuery(id+"F8.wireOp",EDGE,"E211"),sQuery(id+"F8.wireOp",EDGE,"E209"),sQuery(id+"F8.wireOp",EDGE,"E210"),sQuery(id+"F8.wireOp",EDGE,"E205.MirrorCS"),sQuery(id+"F8.wireOp",EDGE,"E217"),sQuery(id+"F8.wireOp",EDGE,"E212"),sQuery(id+"F8.wireOp",EDGE,"E213"),sQuery(id+"F8.wireOp",EDGE,"E214"),sQuery(id+"F8.wireOp",EDGE,"E215"),sQuery(id+"F8.wireOp",EDGE,"E216")])]});
            transform(context, id + "F16", {"entities" : qUnion([Q0]), "transformType" : TransformType.TRANSLATION_3D, "dx" : 0 * mm, "dy" : 0 * mm, "dz" : 3.3 * mm, "makeCopy" : false});
        }
    });
